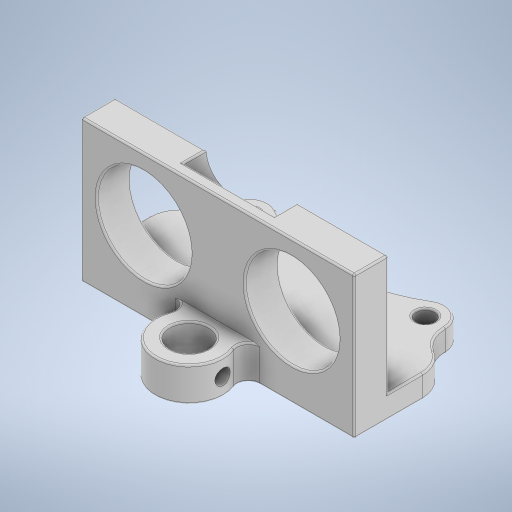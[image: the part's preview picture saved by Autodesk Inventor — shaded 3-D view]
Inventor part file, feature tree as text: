
AUTODESK INVENTOR PART (.ipt)
format: ipt  version: 2023 (Build 270158000, 158)  size: 481,792 bytes
history: native  units: in
note: dims shown in document units (in); Inventor stores cm internally (conversion verified against a paired STEP export)
features: extrude x7, sketch x7, fillet x1
ambient origin geometry x8: Origin, YZ Plane, XZ Plane, XY Plane, X Axis, Y Axis, Z Axis, Center Point
bodies: Solid1 (feature_tree)
feature tree (15):
  extrude  "Extrusion1"  Depth=1.2205in
  extrude  "Extrusion3"  Depth=0.1969in
  extrude  "Extrusion4"  Depth=0.8268in
  extrude  "Extrusion5"  Depth=0.2677in
  extrude  "Extrusion6"  Depth=0.1969in
  extrude  "Extrusion7"  Depth=0.1969in
  extrude  "Extrusion8"  Depth=0.0118in
  fillet  "Fillet1"  Radius=0.8268in
  sketch  "Sketch1"  dims[d0=0.1299in d1=1.2205in]
  sketch  "Sketch3"  dims[d3=0.1378in d6=0.1969in]
  sketch  "Sketch4"  dims[d8=0.1181in d10=0.8268in]
  sketch  "Sketch5"  dims[d11=0.4724in d12=0.2677in]
  sketch  "Sketch6"  dims[d13=0.1969in d14=0.2362in d15=1.8898in]
  sketch  "Sketch7"  dims[d16=0.1969in d17=0.0787in]
  sketch  "Sketch8"  dims[d19=0.1575in d20=0.0in d23=0.2362in d24=0.8268in d25=0.0in d26=1.0236in d27=0.6496in d28=0.5118in d29=0.3937in d30=0.0in d31=0.0in d32=0.4528in d33=0.1969in d34=0.3839in d35=0.1575in d36=0.0in d37=0.6299in d38=0.3543in d39=0.1575in d40=0.0in d41=0.0787in d42=0.0in d43=0.1063in d44=0.1181in d45=0.9449in d46=0.0in d47=0.0118in]
